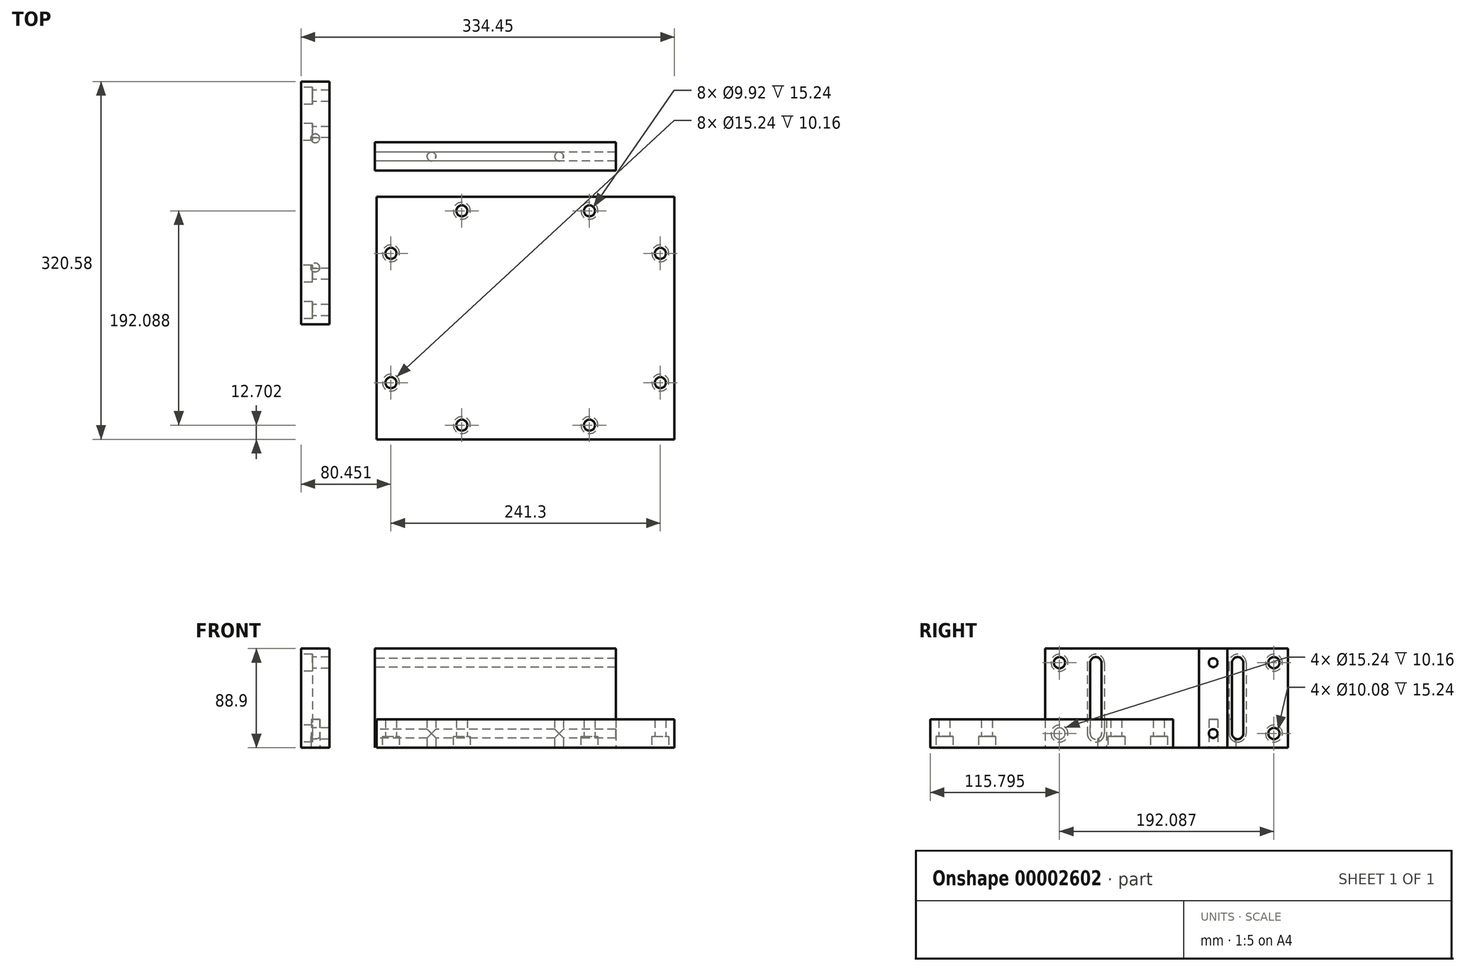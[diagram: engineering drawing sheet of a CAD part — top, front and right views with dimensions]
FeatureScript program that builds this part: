
annotation { "Feature Type Name" : "Feature", "Feature Type Description" : "" }
export const myFeature = defineFeature(function(context is Context, id is Id, definition is map)
    precondition{}
    {
        {
            var Q0;
            Q0=qCreatedBy(makeId("Top.planeOp"),FACE);
            var sketch = newSketch(context, id + "F0", { "sketchPlane" : qUnion([Q0])});
            skLineSegment(sketch, "E0.bottom", {"start": v(-80.08, 160.23) * mm, "end": v(-54.68, 160.23) * mm});
            skLineSegment(sketch, "E0.top", {"start": v(-80.08, -57.26) * mm, "end": v(-54.68, -57.26) * mm});
            skLineSegment(sketch, "E0.left", {"start": v(-80.08, 160.23) * mm, "end": v(-80.08, -57.26) * mm});
            skLineSegment(sketch, "E0.right", {"start": v(-54.68, 160.23) * mm, "end": v(-54.68, -57.26) * mm});
            skSolve(sketch);
        }
        {
            var Q0;
            Q0 = qSketchRegion(id + "F0", true);
            extrude(context, id + "F1", {"entities" : qUnion([Q0]), "depth" : 88.9 * mm});
        }
        {
            var Q0;
            Q0=qCreatedBy(makeId("Top.planeOp"),FACE);
            var sketch = newSketch(context, id + "F2", { "sketchPlane" : qUnion([Q0])});
            skLineSegment(sketch, "E1.bottom", {"start": v(-14.12, 105.82) * mm, "end": v(201.78, 105.82) * mm});
            skLineSegment(sketch, "E1.top", {"start": v(-14.12, 80.42) * mm, "end": v(201.78, 80.42) * mm});
            skLineSegment(sketch, "E1.left", {"start": v(-14.12, 105.82) * mm, "end": v(-14.12, 80.42) * mm});
            skLineSegment(sketch, "E1.right", {"start": v(201.78, 105.82) * mm, "end": v(201.78, 80.42) * mm});
            skSolve(sketch);
        }
        {
            var Q0;
            Q0 = qSketchRegion(id + "F2", true);
            extrude(context, id + "F3", {"entities" : qUnion([Q0]), "depth" : 88.9 * mm});
        }
        {
            var Q0;
            Q0=makeQuery(id+"F3.opExtrude","SWEPT_FACE",FACE,{"disambiguationData":[OSD([sQuery(id+"F2.wireOp",EDGE,"E1.left")])]});
            var sketch = newSketch(context, id + "F4", { "sketchPlane" : qUnion([Q0])});
            skCircle(sketch, "E2", {"center": v(-93.12, 76.2) * mm, "radius": 3.97 * mm});
            skCircle(sketch, "E3", {"center": v(-93.12, 12.7) * mm, "radius": 3.97 * mm});
            skSolve(sketch);
        }
        {
            var Q0;
            Q0 = qSketchRegion(id + "F4", true);
            extrude(context, id + "F5", {"entities" : qUnion([Q0]), "operationType" : NewBodyOperationType.REMOVE, "endBound" : BoundingType.THROUGH_ALL, "oppositeDirection" : true, "depth" : 25.4 * mm});
        }
        {
            var Q0;
            Q0=makeQuery(id+"F1.opExtrude","SWEPT_FACE",FACE,{"disambiguationData":[OSD([sQuery(id+"F0.wireOp",EDGE,"E0.left")])]});
            var sketch = newSketch(context, id + "F6", { "sketchPlane" : qUnion([Q0])});
            skCircle(sketch, "E4", {"center": v(-147.53, 76.2) * mm, "radius": 7.62 * mm});
            skCircle(sketch, "E5", {"center": v(-147.53, 12.7) * mm, "radius": 7.62 * mm});
            skLineSegment(sketch, "E6", {"start": v(-51.49, 88.9) * mm, "end": v(-51.49, 0) * mm, "construction": true});
            skCircle(sketch, "E7.0.MirrorC", {"center": v(44.56, 76.2) * mm, "radius": 7.62 * mm});
            skCircle(sketch, "E8.0.MirrorC", {"center": v(44.56, 12.7) * mm, "radius": 7.62 * mm});
            skCircle(sketch, "E9", {"center": v(-114.99, 76.2) * mm, "radius": 7.62 * mm});
            skCircle(sketch, "E10", {"center": v(-114.99, 12.7) * mm, "radius": 7.62 * mm});
            skLineSegment(sketch, "E11", {"start": v(-122.6, 76.2) * mm, "end": v(-122.6, 12.7) * mm});
            skLineSegment(sketch, "E12", {"start": v(-107.37, 76.2) * mm, "end": v(-107.37, 12.7) * mm});
            skCircle(sketch, "E13.0.MirrorC", {"center": v(12.01, 76.2) * mm, "radius": 7.62 * mm});
            skLineSegment(sketch, "E14.0.MirrorCS", {"start": v(4.4, 76.2) * mm, "end": v(4.4, 12.7) * mm});
            skLineSegment(sketch, "E15.0.MirrorCS", {"start": v(19.63, 76.2) * mm, "end": v(19.63, 12.7) * mm});
            skCircle(sketch, "E16.0.MirrorC", {"center": v(12.01, 12.7) * mm, "radius": 7.62 * mm});
            skSolve(sketch);
        }
        {
            var Q0;
            Q0 = qSketchRegion(id + "F6", true);
            extrude(context, id + "F7", {"entities" : qUnion([Q0]), "operationType" : NewBodyOperationType.REMOVE, "oppositeDirection" : true, "depth" : 10.16 * mm});
        }
        {
            var Q0;
            Q0=makeQuery(id+"F7.boolean.opBoolean","COPY",FACE,{"derivedFrom":makeQuery(id+"F7.opExtrude","CAP_FACE",FACE,{"disambiguationData":[OSD([sQuery(id+"F6.wireOp",EDGE,"E4")])],"isStart":false})});
            var sketch = newSketch(context, id + "F8", { "sketchPlane" : qUnion([Q0])});
            skCircle(sketch, "E17", {"center": v(-147.53, 76.2) * mm, "radius": 5.04 * mm});
            skCircle(sketch, "E18", {"center": v(-147.53, 12.7) * mm, "radius": 5.04 * mm});
            skLineSegment(sketch, "E19", {"start": v(-51.49, 88.9) * mm, "end": v(-51.49, 0) * mm, "construction": true});
            skCircle(sketch, "E20.0.MirrorC", {"center": v(44.56, 76.2) * mm, "radius": 5.04 * mm});
            skCircle(sketch, "E21.0.MirrorC", {"center": v(44.56, 12.7) * mm, "radius": 5.04 * mm});
            skCircle(sketch, "E22", {"center": v(-114.99, 76.2) * mm, "radius": 5.04 * mm});
            skCircle(sketch, "E23", {"center": v(-114.99, 12.7) * mm, "radius": 5.04 * mm});
            skLineSegment(sketch, "E24", {"start": v(-109.95, 12.7) * mm, "end": v(-109.95, 76.2) * mm});
            skLineSegment(sketch, "E25", {"start": v(-120.03, 12.7) * mm, "end": v(-120.03, 76.2) * mm});
            skCircle(sketch, "E26.0.MirrorC", {"center": v(12.01, 76.2) * mm, "radius": 5.04 * mm});
            skLineSegment(sketch, "E27.0.MirrorCS", {"start": v(6.97, 12.7) * mm, "end": v(6.97, 76.2) * mm});
            skLineSegment(sketch, "E28.0.MirrorCS", {"start": v(17.05, 12.7) * mm, "end": v(17.05, 76.2) * mm});
            skCircle(sketch, "E29.0.MirrorC", {"center": v(12.01, 12.7) * mm, "radius": 5.04 * mm});
            skSolve(sketch);
        }
        {
            var Q0;
            Q0 = qSketchRegion(id + "F8", true);
            extrude(context, id + "F9", {"entities" : qUnion([Q0]), "operationType" : NewBodyOperationType.REMOVE, "endBound" : BoundingType.THROUGH_ALL, "oppositeDirection" : true, "depth" : 25.4 * mm});
        }
        {
            var Q0;
            Q0=qCreatedBy(makeId("Top.planeOp"),FACE);
            var sketch = newSketch(context, id + "F10", { "sketchPlane" : qUnion([Q0])});
            skLineSegment(sketch, "E30.bottom", {"start": v(-12.33, 57.14) * mm, "end": v(254.37, 57.14) * mm});
            skLineSegment(sketch, "E30.top", {"start": v(-12.33, -160.35) * mm, "end": v(254.37, -160.35) * mm});
            skLineSegment(sketch, "E30.left", {"start": v(-12.33, 57.14) * mm, "end": v(-12.33, -160.35) * mm});
            skLineSegment(sketch, "E30.right", {"start": v(254.37, 57.14) * mm, "end": v(254.37, -160.35) * mm});
            skCircle(sketch, "E31", {"center": v(0.37, 6.34) * mm, "radius": 4.96 * mm});
            skCircle(sketch, "E32", {"center": v(0.37, -109.55) * mm, "radius": 4.96 * mm});
            skCircle(sketch, "E33", {"center": v(63.87, 44.44) * mm, "radius": 4.96 * mm});
            skCircle(sketch, "E34", {"center": v(178.17, 44.44) * mm, "radius": 4.96 * mm});
            skCircle(sketch, "E35", {"center": v(241.67, 6.34) * mm, "radius": 4.96 * mm});
            skCircle(sketch, "E36", {"center": v(241.67, -109.55) * mm, "radius": 4.96 * mm});
            skCircle(sketch, "E37", {"center": v(178.17, -147.65) * mm, "radius": 4.96 * mm});
            skCircle(sketch, "E38", {"center": v(63.87, -147.65) * mm, "radius": 4.96 * mm});
            skSolve(sketch);
        }
        {
            var Q0;
            Q0 = qSketchRegion(id + "F10", true);
            extrude(context, id + "F11", {"entities" : qUnion([Q0]), "depth" : 25.4 * mm});
        }
        {
            var Q0;
            Q0=makeQuery(id+"F11.opExtrude","CAP_FACE",FACE,{"disambiguationData":[OSD([sQuery(id+"F10.wireOp",EDGE,"E30.bottom"),sQuery(id+"F10.wireOp",EDGE,"E30.top"),sQuery(id+"F10.wireOp",EDGE,"E30.left"),sQuery(id+"F10.wireOp",EDGE,"E30.right"),sQuery(id+"F10.wireOp",EDGE,"E31"),sQuery(id+"F10.wireOp",EDGE,"E32"),sQuery(id+"F10.wireOp",EDGE,"E33"),sQuery(id+"F10.wireOp",EDGE,"E34"),sQuery(id+"F10.wireOp",EDGE,"E35"),sQuery(id+"F10.wireOp",EDGE,"E36"),sQuery(id+"F10.wireOp",EDGE,"E37"),sQuery(id+"F10.wireOp",EDGE,"E38")])],"isStart":true});
            var sketch = newSketch(context, id + "F12", { "sketchPlane" : qUnion([Q0])});
            skCircle(sketch, "E39", {"center": v(63.87, 147.65) * mm, "radius": 7.62 * mm});
            skCircle(sketch, "E40", {"center": v(178.17, 147.65) * mm, "radius": 7.62 * mm});
            skCircle(sketch, "E41", {"center": v(241.67, 109.55) * mm, "radius": 7.62 * mm});
            skCircle(sketch, "E42", {"center": v(241.67, -6.34) * mm, "radius": 7.62 * mm});
            skCircle(sketch, "E43", {"center": v(178.17, -44.44) * mm, "radius": 7.62 * mm});
            skCircle(sketch, "E44", {"center": v(63.87, -44.44) * mm, "radius": 7.62 * mm});
            skCircle(sketch, "E45", {"center": v(0.37, -6.34) * mm, "radius": 7.62 * mm});
            skCircle(sketch, "E46", {"center": v(0.37, 109.55) * mm, "radius": 7.62 * mm});
            skSolve(sketch);
        }
        {
            var Q0;
            Q0 = qSketchRegion(id + "F12", true);
            extrude(context, id + "F13", {"entities" : qUnion([Q0]), "operationType" : NewBodyOperationType.REMOVE, "oppositeDirection" : true, "depth" : 10.16 * mm});
        }
        {
            var Q0;
            Q0=makeQuery(id+"F1.opExtrude","CAP_FACE",FACE,{"disambiguationData":[OSD([sQuery(id+"F0.wireOp",EDGE,"E0.bottom"),sQuery(id+"F0.wireOp",EDGE,"E0.top"),sQuery(id+"F0.wireOp",EDGE,"E0.left"),sQuery(id+"F0.wireOp",EDGE,"E0.right")])],"isStart":true});
            var sketch = newSketch(context, id + "F14", { "sketchPlane" : qUnion([Q0])});
            skCircle(sketch, "E47", {"center": v(-67.38, -109.43) * mm, "radius": 3.97 * mm});
            skCircle(sketch, "E48", {"center": v(-67.38, 6.46) * mm, "radius": 3.97 * mm});
            skSolve(sketch);
        }
        {
            var Q0;
            Q0 = qSketchRegion(id + "F14", true);
            extrude(context, id + "F15", {"entities" : qUnion([Q0]), "operationType" : NewBodyOperationType.REMOVE, "oppositeDirection" : true, "depth" : 25.4 * mm});
        }
        {
            var Q0;
            Q0=makeQuery(id+"F3.opExtrude","CAP_FACE",FACE,{"disambiguationData":[OSD([sQuery(id+"F2.wireOp",EDGE,"E1.bottom"),sQuery(id+"F2.wireOp",EDGE,"E1.top"),sQuery(id+"F2.wireOp",EDGE,"E1.left"),sQuery(id+"F2.wireOp",EDGE,"E1.right")])],"isStart":true});
            var sketch = newSketch(context, id + "F16", { "sketchPlane" : qUnion([Q0])});
            skCircle(sketch, "E49", {"center": v(150.98, -93.12) * mm, "radius": 3.97 * mm});
            skCircle(sketch, "E50", {"center": v(36.68, -93.12) * mm, "radius": 3.97 * mm});
            skSolve(sketch);
        }
        {
            var Q0;
            Q0 = qSketchRegion(id + "F16", true);
            extrude(context, id + "F17", {"entities" : qUnion([Q0]), "operationType" : NewBodyOperationType.REMOVE, "oppositeDirection" : true, "depth" : 25.4 * mm});
        }
    });
